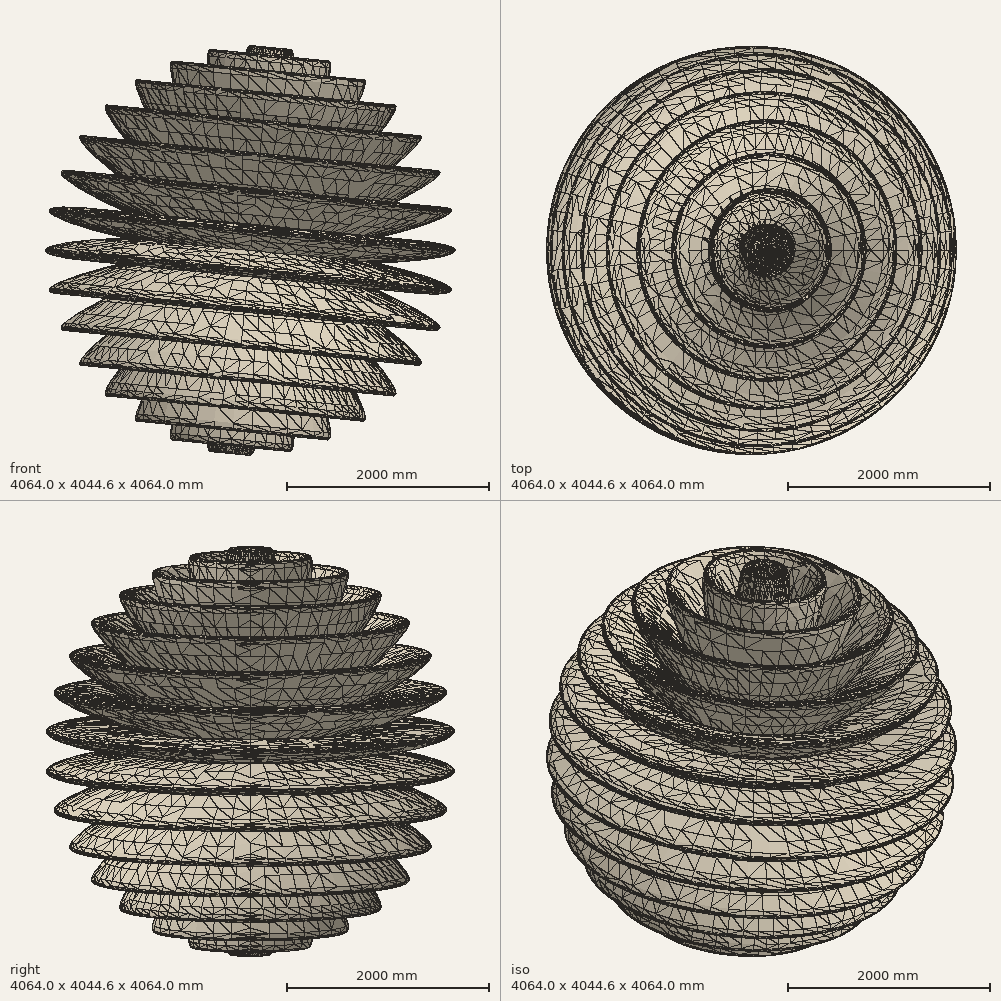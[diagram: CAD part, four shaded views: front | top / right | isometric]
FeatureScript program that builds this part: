
annotation { "Feature Type Name" : "Feature", "Feature Type Description" : "" }
export const myFeature = defineFeature(function(context is Context, id is Id, definition is map)
    precondition{}
    {
        {
            var Q0;
            Q0=qCreatedBy(makeId("Front.planeOp"),FACE);
            var sketch = newSketch(context, id + "F0", { "sketchPlane" : qUnion([Q0])});
            skEllipticalArc(sketch, "E0", {});
            skEllipticalArc(sketch, "E1", {});
            skEllipticalArc(sketch, "E2.MirrorC", {});
            skEllipticalArc(sketch, "E3.MirrorC", {});
            skEllipticalArc(sketch, "E4.MirrorC", {});
            skEllipticalArc(sketch, "E5.MirrorC", {});
            skEllipticalArc(sketch, "E6.MirrorC", {});
            skEllipticalArc(sketch, "E7.MirrorC", {});
            skEllipticalArc(sketch, "E8.MirrorC", {});
            skEllipticalArc(sketch, "E9.MirrorC", {});
            skEllipticalArc(sketch, "E10.MirrorC", {});
            skEllipticalArc(sketch, "E11.MirrorC", {});
            skEllipticalArc(sketch, "E12.MirrorC", {});
            skEllipticalArc(sketch, "E13.MirrorC", {});
            skEllipticalArc(sketch, "E14.MirrorC", {});
            skLineSegment(sketch, "E15", {"start": v(215.43, 2187.25) * mm, "end": v(-209.65, -2128.58) * mm});
            skEllipticalArc(sketch, "E16.trimOffspring", {});
            skEllipticalArc(sketch, "E17.trimOffspring", {});
            skEllipticalArc(sketch, "E18.trimOffspring", {});
            skEllipticalArc(sketch, "E19.trimOffspring", {});
            skEllipticalArc(sketch, "E20.trimOffspring", {});
            skEllipticalArc(sketch, "E21.trimOffspring", {});
            skEllipticalArc(sketch, "E22.trimOffspring", {});
            skEllipticalArc(sketch, "E23.trimOffspring", {});
            skEllipticalArc(sketch, "E24.trimOffspring", {});
            skEllipticalArc(sketch, "E25.trimOffspring", {});
            skEllipticalArc(sketch, "E26.trimOffspring", {});
            skEllipticalArc(sketch, "E27.trimOffspring", {});
            skEllipticalArc(sketch, "E28.trimOffspring", {});
            skEllipticalArc(sketch, "E29.trimOffspring", {});
            skEllipticalArc(sketch, "E30.trimOffspring", {});
            skEllipticalArc(sketch, "E31.trimOffspring", {});
            skEllipticalArc(sketch, "E32.trimOffspring", {});
            const initialGuessF0  = {"E0": [-0.5644593567482208, 0.8447731260974697, 0.5555702330196016, -0.8314696123025457, 1.016, 0.127, 0.30230244236289405, 0], "E1": [-0.3888063672834946, 0.9386616050311986, 0.38268343236515195, -0.923879532511261, 1.016, 0.127, 0.4594599494956132, 1.0380934956788403e-10], "E2.MirrorC": [0, 1.016, 0, -1, 1.016, 0.127, 1.806915675883518, 1.2523582171297676e-10], "E3.MirrorC": [0.1982117671635813, 0.9964778448907797, -0.19509032201172347, -0.9807852804041067, 1.016, 0.127, 4.476269631299923, 0], "E4.MirrorC": [0.388806367283029, 0.9386616050359327, -0.3826834323649473, -0.9238795325113458, 1.016, 0.127, 5.501449587669666, 0], "E5.MirrorC": [0.5644593567474829, 0.8447731261002971, -0.5555702330193586, -0.8314696123027081, 1.016, 0.127, 5.823725357684941, 0], "E6.MirrorC": [-0.198211767167673, 0.9964778448941444, 0.19509032201532292, -0.9807852804033907, 1.016, 0.127, 0.7817357195426219, 0], "E7.MirrorC": [-0.9386616050311214, 0.38880636728268403, 0.9238795325109722, -0.3826834323658493, 1.016, 0.127, 0.07580035625631361, 0], "E8.MirrorC": [-0.8447731260909296, 0.5644593567483827, 0.8314696123020889, -0.5555702330202852, 1.016, 0.127, 0.13342947253038692, 0], "E9.MirrorC": [-0.9964778448937222, 0.1982117671632642, 0.9807852804032303, -0.19509032201612916, 1.016, 0.127, 0.024621606850201736, 1.9346838217210293e-10], "E10.MirrorC": [-1.016, 0, 1, 0, 1.016, 0.127, 6.283185307167621, 6.258563700275284], "E11.MirrorC": [-0.718420489685427, 0.7184204896855583, 0.707106781186548, -0.7071067811865471, 1.016, 0.127, 0.20445449677467392, 1.3133676123908026e-10], "E12.MirrorC": [-0.5644593567485473, -0.8447731260992025, 0.5555702330196026, 0.8314696123025451, 1.016, 0.127, 6.283185307176878, 5.823725357694929], "E13.MirrorC": [-0.9386616050332609, -0.3888063672827329, 0.9238795325112868, 0.38268343236508967, 1.016, 0.127, 6.2831853071719435, 6.149755834749218], "E14.MirrorC": [-0.9964778448894682, -0.19821176716594016, 0.980785280403223, 0.1950903220161666, 1.016, 0.127, 6.283185307166434, 6.20738495094672], "E16.trimOffspring": [0.7184204896853152, 0.7184204896847759, -0.7071067811865488, -0.7071067811865465, 1.016, 0.127, 5.9808828648143955, 0], "E17.trimOffspring": [0.8447731260992, 0.5644593567479533, -0.8314696123024582, -0.5555702330197326, 1.016, 0.127, 6.078730810404285, 0], "E18.trimOffspring": [1.016, 0, -1, 0, 1.016, 0.127, 6.258563700314891, 0], "E19.trimOffspring": [0.9964778448903715, 0.19821176716863292, -0.9807852804032199, -0.19509032201618168, 1.016, 0.127, 6.207384950960419, 0], "E20.trimOffspring": [0.9386616050316471, 0.3888063672820382, -0.9238795325112876, -0.38268343236508784, 1.016, 0.127, 6.149755834719876, 0], "E21.trimOffspring": [0.996477844888828, -0.19821176717301556, -0.9807852804022056, 0.1950903220212808, 1.016, 0.127, 6.283185307036853, 0.024621606909547813], "E22.trimOffspring": [-0.19821176716838118, -0.9964778448885921, 0.1950903220161278, 0.9807852804032307, 1.016, 0.127, 6.283185307161855, 4.476269631302108], "E23.trimOffspring": [0, -1.016, 0, 1, 1.016, 0.127, 6.2831853071436505, 1.806915675879062], "E24.trimOffspring": [0.19821176717330447, -0.9964778448879634, -0.1950903220210339, 0.9807852804022547, 1.016, 0.127, 6.2831853071734605, 0.7817357195098565], "E25.trimOffspring": [0.38880636728513485, -0.9386616050273677, -0.38268343236597374, 0.9238795325109207, 1.016, 0.127, 6.283185307178126, 0.459459949489489], "E26.trimOffspring": [0.5644593567561399, -0.8447731261178876, -0.5555702330196016, 0.8314696123025457, 1.016, 0.127, 6.283185307173793, 0.3023024423987785], "E27.trimOffspring": [0.7184204896966949, -0.7184204897041196, -0.7071067811865464, 0.7071067811865488, 1.016, 0.127, 6.283185307169054, 0.20445449721239056], "E28.trimOffspring": [0.8447731260989674, -0.5644593567544598, -0.8314696123007451, 0.5555702330222964, 1.016, 0.127, 6.283185307162053, 0.13342947242946976], "E29.trimOffspring": [0.9386616050460519, -0.3888063672898612, -0.9238795325113119, 0.382683432365029, 1.016, 0.127, 6.283185307160542, 0.07580035610320622], "E30.trimOffspring": [-0.8447731260984064, -0.5644593567461861, 0.8314696123025458, 0.5555702330196015, 1.016, 0.127, 6.283185307169829, 6.078730810383758], "E31.trimOffspring": [-0.7184204896839816, -0.7184204896865519, 0.7071067811865474, 0.7071067811865478, 1.016, 0.127, 6.283185307171032, 5.980882864813811], "E32.trimOffspring": [-0.3888063672815328, -0.938661605030874, 0.3826834323650883, 0.9238795325112874, 1.016, 0.127, 6.283185307175501, 5.501449587669715]};
            skSetInitialGuess(sketch, initialGuessF0);
            skSolve(sketch);
        }
        {
            var Q0;
            Q0=qSketchRegion(id+"F0",true);
            var Q1;
            Q1 = qConstructionFilter(qBodyType(qCreatedBy(id + "F0" ,EDGE), BodyType.WIRE), ConstructionObject.NO);
            var Q2;
            Q2=sQuery(id+"F0.wireOp",EDGE,"E15");
            revolve(context, id + "F1", {"entities" : qUnion([Q0]), "surfaceEntities" : qUnion([Q1]), "axis" : qUnion([Q2]), "revolveType" : RevolveType.FULL});
        }
    });
